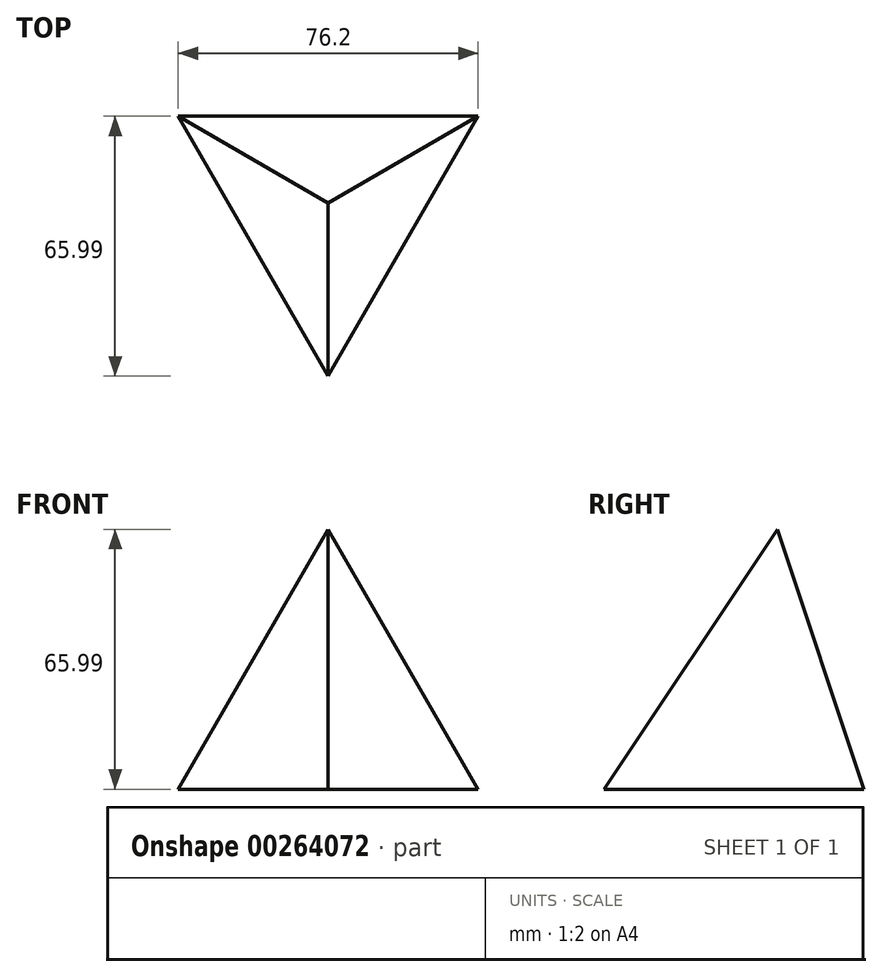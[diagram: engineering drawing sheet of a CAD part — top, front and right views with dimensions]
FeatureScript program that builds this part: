
annotation { "Feature Type Name" : "Feature", "Feature Type Description" : "" }
export const myFeature = defineFeature(function(context is Context, id is Id, definition is map)
    precondition{}
    {
        {
            var Q0;
            Q0=qCreatedBy(makeId("Top.planeOp"),FACE);
            var sketch = newSketch(context, id + "F0", { "sketchPlane" : qUnion([Q0])});
            skLineSegment(sketch, "E0", {"start": v(-38.1, 22) * mm, "end": v(0, -44) * mm});
            skLineSegment(sketch, "E1", {"start": v(0, -44) * mm, "end": v(38.1, 22) * mm});
            skLineSegment(sketch, "E2", {"start": v(38.1, 22) * mm, "end": v(-38.1, 22) * mm});
            skPoint(sketch, "E3", {"position": v(-19.05, -11) * mm});
            skSolve(sketch);
        }
        {
            var Q0;
            Q0=qCreatedBy(makeId("Front.planeOp"),FACE);
            var sketch = newSketch(context, id + "F1", { "sketchPlane" : qUnion([Q0])});
            skPoint(sketch, "E4", {"position": v(0, 65.99) * mm});
            skSolve(sketch);
        }
        {
            var Q0;
            Q0=makeQuery(id+"F0.imprint","IMPRINT",FACE,{"disambiguationData":[TD([[makeQuery(id+"F0.imprint","IMPRINT",EDGE,{"derivedFrom":sQuery(id+"F0.wireOp",EDGE,"E0")}),1.0]])]});
            var Q1;
            Q1=sQuery(id+"F1.wireOp",VERTEX,"E4");
            loft(context, id + "F2", {"sheetProfilesArray" : [{ "sheetProfileEntities" : qUnion([Q0]) }, { "sheetProfileEntities" : qUnion([Q1]) }]});
        }
    });
